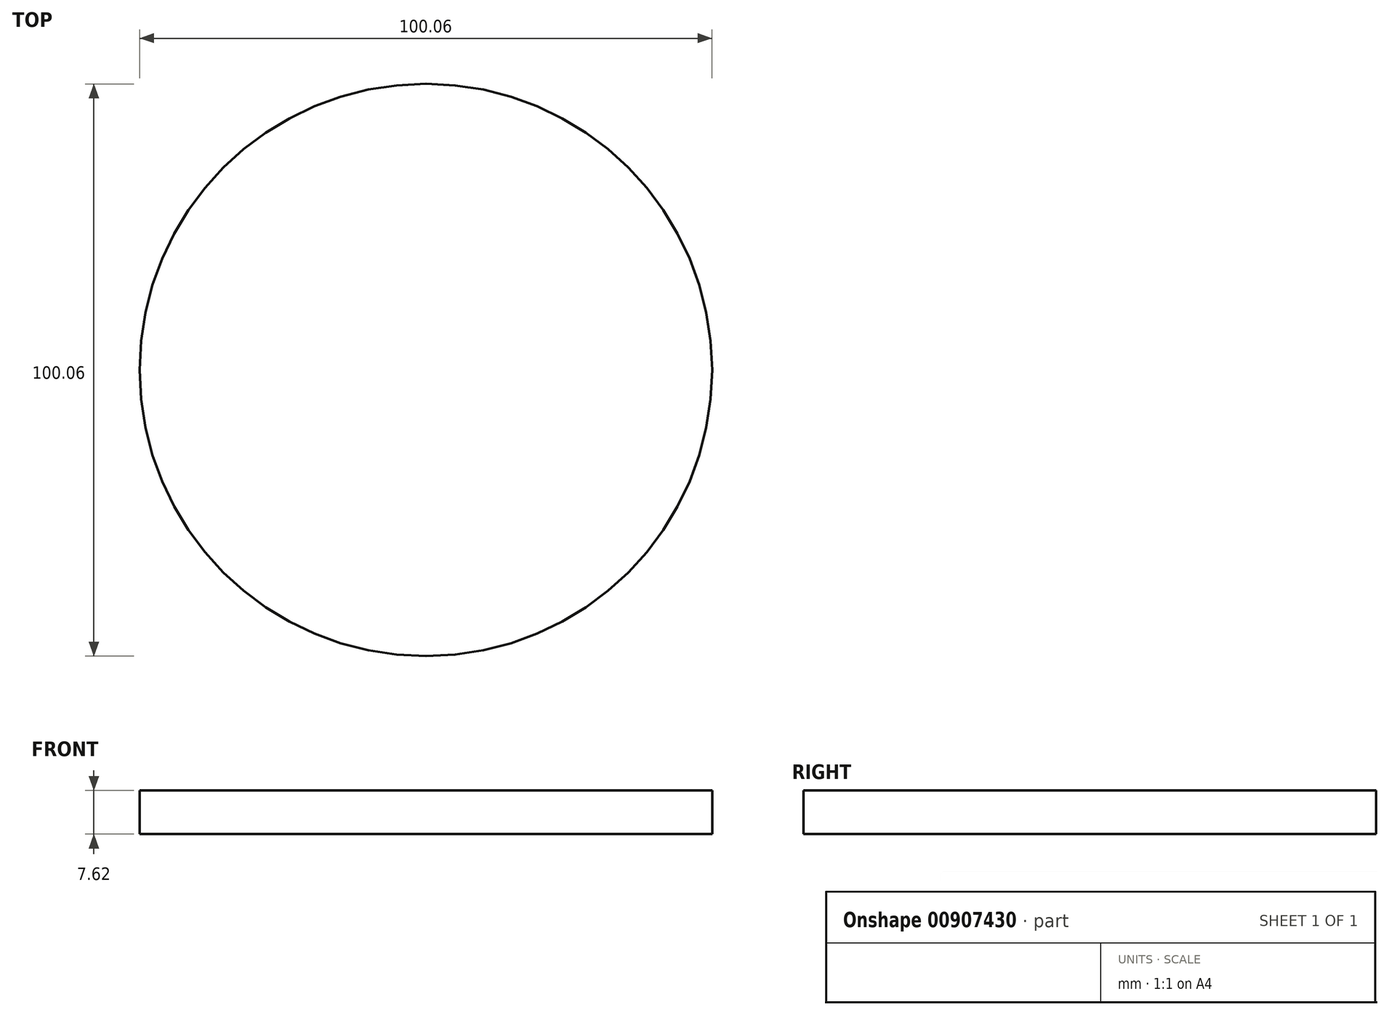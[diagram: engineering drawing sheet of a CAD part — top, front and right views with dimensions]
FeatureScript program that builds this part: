
annotation { "Feature Type Name" : "Feature", "Feature Type Description" : "" }
export const myFeature = defineFeature(function(context is Context, id is Id, definition is map)
    precondition{}
    {
        {
            var Q0;
            Q0=qCreatedBy(makeId("Top.planeOp"),FACE);
            var sketch = newSketch(context, id + "F0", { "sketchPlane" : qUnion([Q0])});
            skCircle(sketch, "E0", {"center": v(0, 0) * mm, "radius": 50.03 * mm});
            skSolve(sketch);
        }
        {
            var Q0;
            Q0 = qSketchRegion(id + "F0", true);
            extrude(context, id + "F1", {"entities" : qUnion([Q0]), "depth" : 7.62 * mm, "offsetDistance" : 25.4 * mm});
        }
    });
